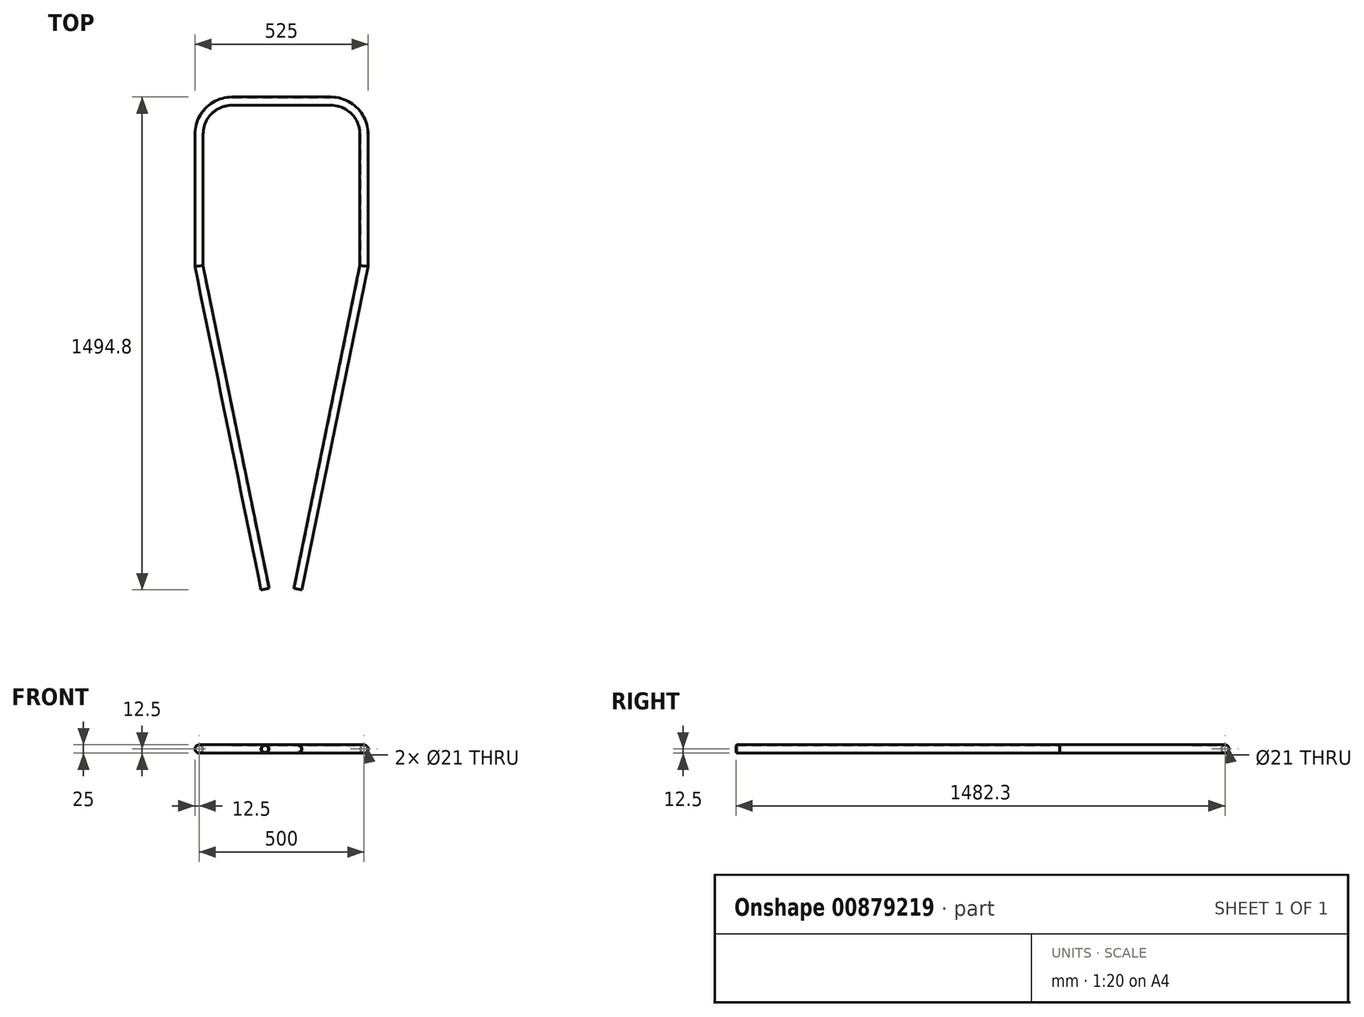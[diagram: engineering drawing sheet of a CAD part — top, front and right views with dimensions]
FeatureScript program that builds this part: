
annotation { "Feature Type Name" : "Feature", "Feature Type Description" : "" }
export const myFeature = defineFeature(function(context is Context, id is Id, definition is map)
    precondition{}
    {
        {
            var Q0;
            Q0=qCreatedBy(makeId("Front.planeOp"),FACE);
            var sketch = newSketch(context, id + "F0", { "sketchPlane" : qUnion([Q0])});
            skCircle(sketch, "E0", {"center": v(0, 0) * mm, "radius": 12.5 * mm});
            skPoint(sketch, "E1", {"position": v(0, 12.5) * mm});
            skCircle(sketch, "E2", {"center": v(0, 0) * mm, "radius": 10.5 * mm});
            skPoint(sketch, "E3", {"position": v(0, 10.5) * mm});
            skPoint(sketch, "E4", {"position": v(0, -12.5) * mm});
            skSolve(sketch);
        }
        {
            var Q0;
            Q0=qCreatedBy(makeId("Top.planeOp"),FACE);
            var sketch = newSketch(context, id + "F1", { "sketchPlane" : qUnion([Q0])});
            skLineSegment(sketch, "E5", {"start": v(0, 0) * mm, "end": v(0, 106) * mm});
            skLineSegment(sketch, "E6", {"start": v(-100, 206) * mm, "end": v(-400, 206) * mm});
            skLineSegment(sketch, "E7", {"start": v(-500, 106) * mm, "end": v(-500, -294) * mm});
            skLineSegment(sketch, "E8", {"start": v(-500, -294) * mm, "end": v(0, -294) * mm});
            skLineSegment(sketch, "E9", {"start": v(0, -294) * mm, "end": v(0, 0) * mm});
            skPoint(sketch, "E10.visualSharp", {"position": v(0, 206) * mm});
            skArc(sketch, "E10.filletArc", {"start": v(0, 106) * mm, "mid": v(-29.29, 176.7) * mm, "end": v(-100, 206) * mm});
            skPoint(sketch, "E11.visualSharp", {"position": v(-500, 206) * mm});
            skArc(sketch, "E11.filletArc", {"start": v(-400, 206) * mm, "mid": v(-470.71, 176.7) * mm, "end": v(-500, 106) * mm});
            skLineSegment(sketch, "E12", {"start": v(-500, -294) * mm, "end": v(-300, -1273.8) * mm});
            skLineSegment(sketch, "E13", {"start": v(0, -294) * mm, "end": v(-200, -1273.8) * mm});
            skSolve(sketch);
        }
        {
            var Q0;
            Q0=makeQuery(id+"F0.imprint","IMPRINT",FACE,{"disambiguationData":[TD([[makeQuery(id+"F0.imprint","IMPRINT",EDGE,{"derivedFrom":sQuery(id+"F0.wireOp",EDGE,"E0")}),1.0]])]});
            var Q1;
            Q1=sQuery(id+"F1.wireOp",EDGE,"E9");
            var Q2;
            Q2=sQuery(id+"F1.wireOp",EDGE,"E5");
            var Q3;
            Q3=sQuery(id+"F1.wireOp",EDGE,"E10.filletArc");
            var Q4;
            Q4=sQuery(id+"F1.wireOp",EDGE,"E6");
            var Q5;
            Q5=sQuery(id+"F1.wireOp",EDGE,"E11.filletArc");
            var Q6;
            Q6=sQuery(id+"F1.wireOp",EDGE,"E7");
            var Q7;
            Q7=sQuery(id+"F1.wireOp",EDGE,"E12");
            var Q8;
            Q8=sQuery(id+"F1.wireOp",EDGE,"E13");
            sweep(context, id + "F2", {"profiles" : qUnion([Q0]), "path" : qUnion([Q1, Q2, Q3, Q4, Q5, Q6, Q7, Q8])});
        }
    });
